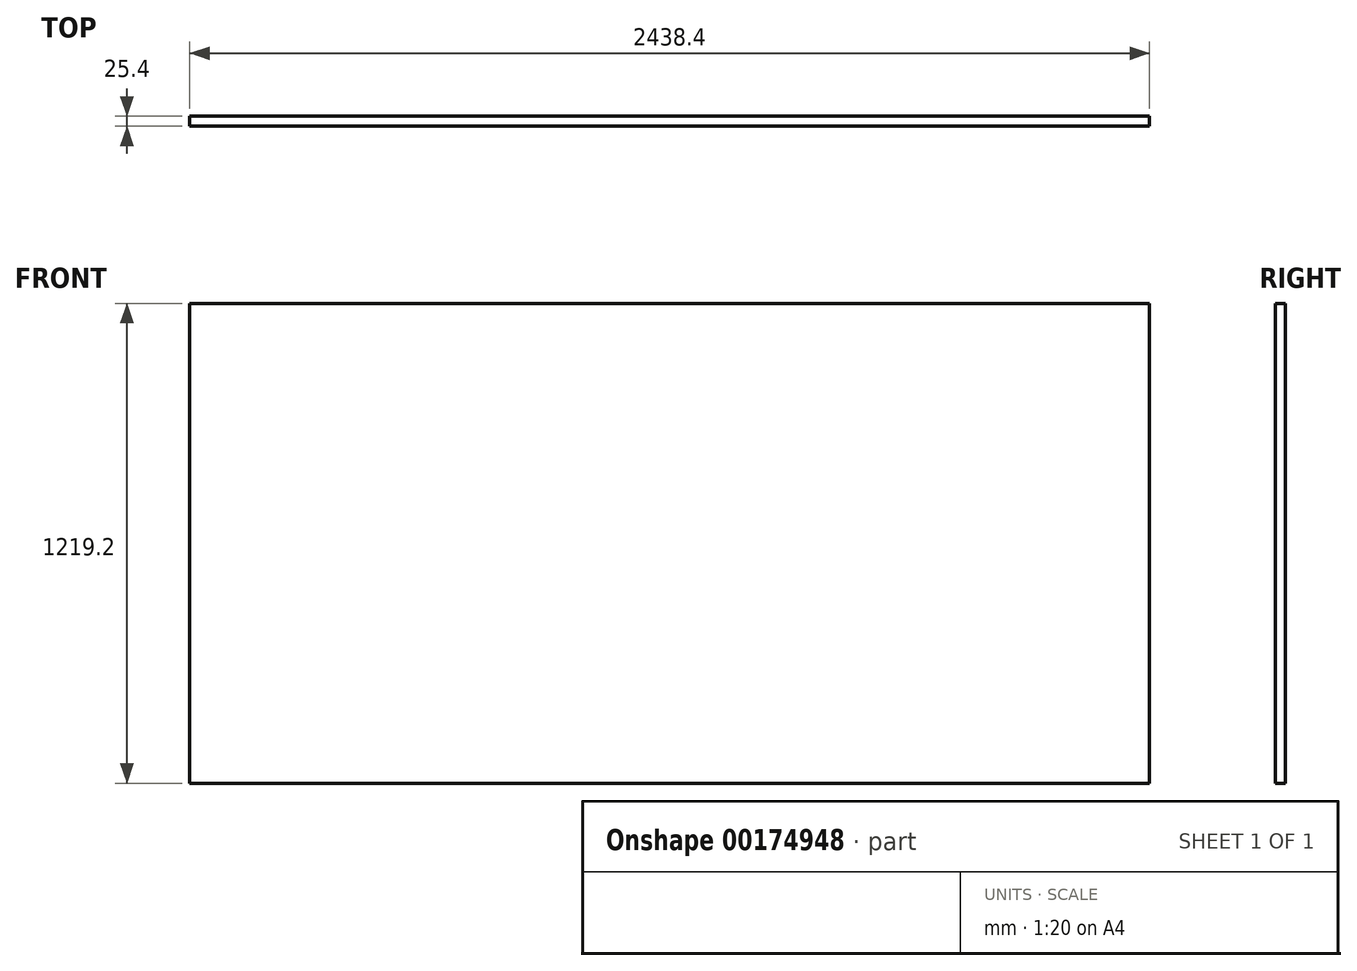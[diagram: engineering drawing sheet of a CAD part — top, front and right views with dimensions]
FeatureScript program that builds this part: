
annotation { "Feature Type Name" : "Feature", "Feature Type Description" : "" }
export const myFeature = defineFeature(function(context is Context, id is Id, definition is map)
    precondition{}
    {
        {
            var Q0;
            Q0=qCreatedBy(makeId("Front.planeOp"),FACE);
            var sketch = newSketch(context, id + "F0", { "sketchPlane" : qUnion([Q0])});
            skLineSegment(sketch, "E0.bottom", {"start": v(1219.2, 609.6) * mm, "end": v(-1219.2, 609.6) * mm});
            skLineSegment(sketch, "E0.top", {"start": v(1219.2, -609.6) * mm, "end": v(-1219.2, -609.6) * mm});
            skLineSegment(sketch, "E0.left", {"start": v(1219.2, 609.6) * mm, "end": v(1219.2, -609.6) * mm});
            skLineSegment(sketch, "E0.right", {"start": v(-1219.2, 609.6) * mm, "end": v(-1219.2, -609.6) * mm});
            skPoint(sketch, "E0.middle", {"position": v(0, 0) * mm});
            skSolve(sketch);
        }
        {
            var Q0;
            Q0=makeQuery(id+"F0.imprint","IMPRINT",FACE,{"disambiguationData":[TD([[makeQuery(id+"F0.imprint","IMPRINT",EDGE,{"derivedFrom":sQuery(id+"F0.wireOp",EDGE,"E0.bottom")}),1.0]])]});
            extrude(context, id + "F1", {"entities" : qUnion([Q0]), "depth" : 25.4 * mm, "offsetDistance" : 25.4 * mm});
        }
    });
